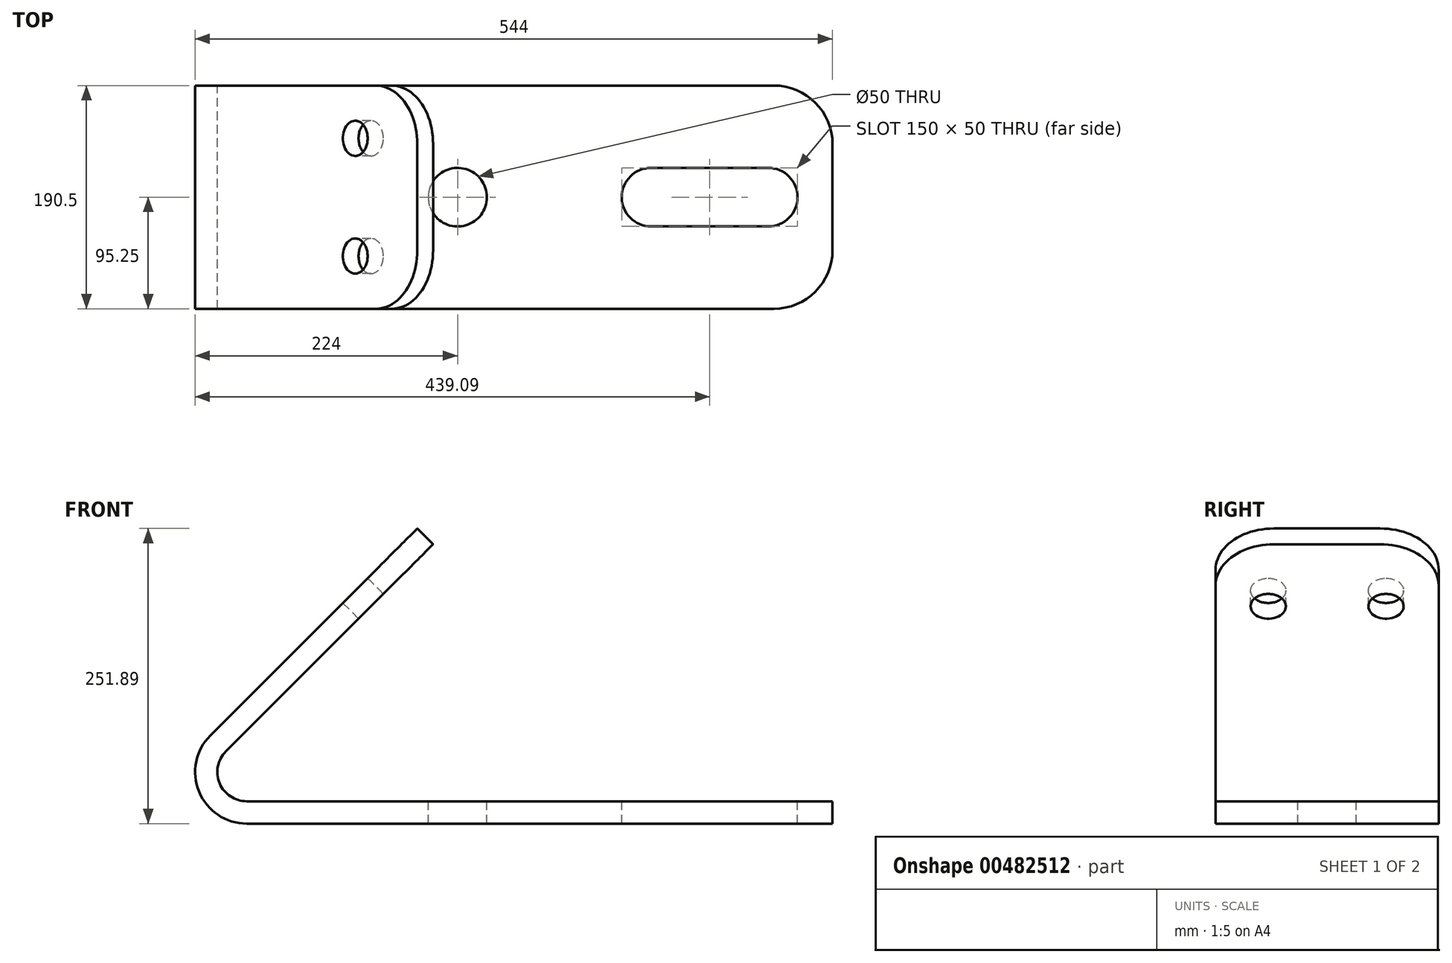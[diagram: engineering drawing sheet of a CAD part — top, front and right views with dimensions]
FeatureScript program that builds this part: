
annotation { "Feature Type Name" : "Feature", "Feature Type Description" : "" }
export const myFeature = defineFeature(function(context is Context, id is Id, definition is map)
    precondition{}
    {
        {
            var Q0;
            Q0=qCreatedBy(makeId("Front.planeOp"),FACE);
            var sketch = newSketch(context, id + "F0", { "sketchPlane" : qUnion([Q0])});
            skArc(sketch, "E0", {"start": v(-31.11, 31.11) * mm, "mid": v(-40.65, -16.84) * mm, "end": v(0, -44) * mm});
            skLineSegment(sketch, "E1", {"start": v(500, -44) * mm, "end": v(0, -44) * mm});
            skLineSegment(sketch, "E2", {"start": v(-31.11, 31.11) * mm, "end": v(145.66, 207.89) * mm});
            skPoint(sketch, "E3", {"position": v(-31.11, 31.11) * mm});
            skPoint(sketch, "E4", {"position": v(0, -44) * mm});
            skLineSegment(sketch, "E5", {"start": v(145.66, 207.89) * mm, "end": v(159.1, 194.45) * mm});
            skLineSegment(sketch, "E6", {"start": v(500, -44) * mm, "end": v(500, -25) * mm});
            skLineSegment(sketch, "E7.0", {"start": v(-17.68, 17.68) * mm, "end": v(159.1, 194.45) * mm});
            skArc(sketch, "E7.1", {"start": v(-17.68, 17.68) * mm, "mid": v(-23.1, -9.57) * mm, "end": v(0, -25) * mm});
            skLineSegment(sketch, "E7.2", {"start": v(500, -25) * mm, "end": v(0, -25) * mm});
            skSolve(sketch);
        }
        {
            var Q0;
            Q0=makeQuery(id+"F0.imprint","IMPRINT",FACE,{"disambiguationData":[TD([[makeQuery(id+"F0.imprint","IMPRINT",EDGE,{"derivedFrom":sQuery(id+"F0.wireOp",EDGE,"E0")}),1.0]])]});
            extrude(context, id + "F1", {"entities" : qUnion([Q0]), "depth" : 190.5 * mm});
        }
        {
            var Q0;
            Q0=makeQuery(id+"F1.opExtrude","CAP_EDGE",EDGE,{"disambiguationData":[OSD([sQuery(id+"F0.wireOp",EDGE,"E6")])],"isStart":true});
            var Q1;
            Q1=makeQuery(id+"F1.opExtrude","CAP_EDGE",EDGE,{"disambiguationData":[OSD([sQuery(id+"F0.wireOp",EDGE,"E6")])],"isStart":false});
            var Q2;
            Q2=makeQuery(id+"F1.opExtrude","CAP_EDGE",EDGE,{"disambiguationData":[OSD([sQuery(id+"F0.wireOp",EDGE,"E5")])],"isStart":false});
            var Q3;
            Q3=makeQuery(id+"F1.opExtrude","CAP_EDGE",EDGE,{"disambiguationData":[OSD([sQuery(id+"F0.wireOp",EDGE,"E5")])],"isStart":true});
            fillet(context, id + "F2", {"entities" : qUnion([Q0, Q1, Q2, Q3]), "radius" : 50 * mm, "tangentPropagation" : true, "allowEdgeOverflow" : false});
        }
        {
            var Q0;
            Q0=makeQuery(id+"F1.opExtrude","SWEPT_FACE",FACE,{"disambiguationData":[OSD([sQuery(id+"F0.wireOp",EDGE,"E7.2")])]});
            var sketch = newSketch(context, id + "F3", { "sketchPlane" : qUnion([Q0])});
            skCircle(sketch, "E8", {"center": v(180, -95.25) * mm, "radius": 25 * mm});
            skPoint(sketch, "E9.start.orphan", {"position": v(500, -95.25) * mm});
            skLineSegment(sketch, "E10.bottom", {"start": v(345.1, -70.25) * mm, "end": v(445.1, -70.25) * mm});
            skLineSegment(sketch, "E10.top", {"start": v(345.1, -120.25) * mm, "end": v(445.1, -120.25) * mm});
            skLineSegment(sketch, "E10.left", {"start": v(320.1, -95.25) * mm, "end": v(320.1, -95.25) * mm});
            skLineSegment(sketch, "E10.right", {"start": v(470.1, -95.25) * mm, "end": v(470.1, -95.25) * mm});
            skArc(sketch, "E11.filletArc", {"start": v(345.1, -70.25) * mm, "mid": v(327.41, -77.57) * mm, "end": v(320.1, -95.25) * mm});
            skArc(sketch, "E12.filletArc", {"start": v(320.1, -95.25) * mm, "mid": v(327.41, -112.93) * mm, "end": v(345.1, -120.25) * mm});
            skArc(sketch, "E13.filletArc", {"start": v(470.1, -95.25) * mm, "mid": v(462.77, -77.57) * mm, "end": v(445.1, -70.25) * mm});
            skArc(sketch, "E14.filletArc", {"start": v(445.1, -120.25) * mm, "mid": v(462.77, -112.93) * mm, "end": v(470.1, -95.25) * mm});
            skSolve(sketch);
        }
        {
            var Q0;
            Q0=makeQuery(id+"F3.imprint","IMPRINT",FACE,{"disambiguationData":[TD([[makeQuery(id+"F3.imprint","IMPRINT",EDGE,{"derivedFrom":sQuery(id+"F3.wireOp",EDGE,"E8")}),1.0]])]});
            extrude(context, id + "F4", {"entities" : qUnion([Q0]), "operationType" : NewBodyOperationType.REMOVE, "oppositeDirection" : true, "depth" : 25 * mm});
        }
        {
            var Q0;
            Q0=makeQuery(id+"F3.imprint","IMPRINT",FACE,{"disambiguationData":[TD([[makeQuery(id+"F3.imprint","IMPRINT",EDGE,{"derivedFrom":sQuery(id+"F3.wireOp",EDGE,"E10.bottom")}),-1.0]])]});
            extrude(context, id + "F5", {"entities" : qUnion([Q0]), "operationType" : NewBodyOperationType.REMOVE, "oppositeDirection" : true, "depth" : 25 * mm});
        }
        {
            var Q0;
            Q0=makeQuery(id+"F1.opExtrude","SWEPT_FACE",FACE,{"disambiguationData":[OSD([sQuery(id+"F0.wireOp",EDGE,"E2")])]});
            var sketch = newSketch(context, id + "F6", { "sketchPlane" : qUnion([Q0])});
            skLineSegment(sketch, "E15", {"start": v(0, 0) * mm, "end": v(45, 0) * mm});
            skLineSegment(sketch, "E16", {"start": v(190.5, 0) * mm, "end": v(145.5, 0) * mm});
            skCircle(sketch, "E17", {"center": v(45, 175) * mm, "radius": 15 * mm});
            skCircle(sketch, "E18", {"center": v(145.5, 175) * mm, "radius": 15 * mm});
            skSolve(sketch);
        }
        {
            var Q0;
            Q0=makeQuery(id+"F6.imprint","IMPRINT",FACE,{"disambiguationData":[TD([[makeQuery(id+"F6.imprint","IMPRINT",EDGE,{"derivedFrom":sQuery(id+"F6.wireOp",EDGE,"E17")}),1.0]])]});
            var Q1;
            Q1=makeQuery(id+"F6.imprint","IMPRINT",FACE,{"disambiguationData":[TD([[makeQuery(id+"F6.imprint","IMPRINT",EDGE,{"derivedFrom":sQuery(id+"F6.wireOp",EDGE,"E18")}),1.0]])]});
            extrude(context, id + "F7", {"entities" : qUnion([Q0, Q1]), "operationType" : NewBodyOperationType.REMOVE, "oppositeDirection" : true, "depth" : 25 * mm});
        }
    });
